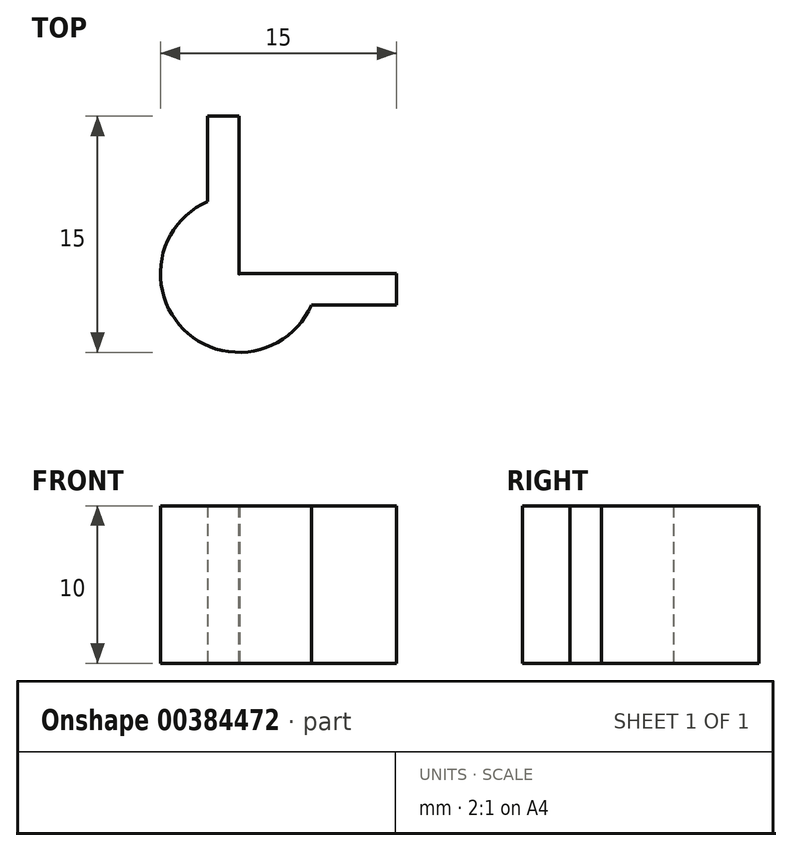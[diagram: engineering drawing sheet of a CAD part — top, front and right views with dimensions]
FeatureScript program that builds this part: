
annotation { "Feature Type Name" : "Feature", "Feature Type Description" : "" }
export const myFeature = defineFeature(function(context is Context, id is Id, definition is map)
    precondition{}
    {
        {
            var Q0;
            Q0=qCreatedBy(makeId("Top.planeOp"),FACE);
            var sketch = newSketch(context, id + "F0", { "sketchPlane" : qUnion([Q0])});
            skLineSegment(sketch, "E0.bottom", {"start": v(0, 0) * mm, "end": v(0, 0) * mm});
            skLineSegment(sketch, "E0.top", {"start": v(0, 0) * mm, "end": v(0, 0) * mm});
            skLineSegment(sketch, "E0.left", {"start": v(0, 0) * mm, "end": v(0, 0) * mm});
            skLineSegment(sketch, "E0.right", {"start": v(0, 0) * mm, "end": v(0, 0) * mm});
            skLineSegment(sketch, "E1.bottom", {"start": v(10, -2) * mm, "end": v(0, -2) * mm});
            skLineSegment(sketch, "E1.top", {"start": v(10, 0) * mm, "end": v(0, 0) * mm});
            skLineSegment(sketch, "E1.left", {"start": v(10, -2) * mm, "end": v(10, 0) * mm});
            skLineSegment(sketch, "E1.right", {"start": v(0, -2) * mm, "end": v(0, 0) * mm});
            skLineSegment(sketch, "E2.bottom", {"start": v(0, 0) * mm, "end": v(-2, 0) * mm});
            skLineSegment(sketch, "E2.top", {"start": v(0, 10) * mm, "end": v(-2, 10) * mm});
            skLineSegment(sketch, "E2.left", {"start": v(0, 0) * mm, "end": v(0, 10) * mm});
            skLineSegment(sketch, "E2.right", {"start": v(-2, 0) * mm, "end": v(-2, 10) * mm});
            skCircle(sketch, "E3", {"center": v(0, 0) * mm, "radius": 0.02 * mm});
            skCircle(sketch, "E4", {"center": v(0, 0) * mm, "radius": 5 * mm});
            skSolve(sketch);
        }
        {
            var Q0;
            {var subQ0=sQuery(id+"F0.wireOp",EDGE,"E2.top");Q0=makeQuery(id+"F0.imprint","IMPRINT",FACE,{"disambiguationData":[TD([[makeQuery(id+"F0.imprint","IMPRINT",EDGE,{"derivedFrom":subQ0}),1.0]])]});}
            var Q1;
            {var subQ0=sQuery(id+"F0.wireOp",EDGE,"E1.left");Q1=makeQuery(id+"F0.imprint","IMPRINT",FACE,{"disambiguationData":[TD([[makeQuery(id+"F0.imprint","IMPRINT",EDGE,{"derivedFrom":subQ0}),1.0]])]});}
            var Q2;
            {var subQ3=sQuery(id+"F0.wireOp",EDGE,"E1.right");var subQ7=sQuery(id+"F0.wireOp",EDGE,"E1.bottom");var subQ8=makeQuery(id+"F0.imprint","INTERSECT",VERTEX,{"derivedFrom":[subQ7,subQ3]});Q2=makeQuery(id+"F0.imprint","IMPRINT",FACE,{"disambiguationData":[TD([[makeQuery(id+"F0.imprint","IMPRINT",EDGE,{"disambiguationData":[TD([[subQ8,1.0]])],"derivedFrom":subQ7}),-1.0]])]});}
            var Q3;
            {var subQ1=sQuery(id+"F0.wireOp",EDGE,"E2.bottom");var subQ7=sQuery(id+"F0.wireOp",EDGE,"E2.right");var subQ8=makeQuery(id+"F0.imprint","INTERSECT",VERTEX,{"derivedFrom":[subQ1,subQ7]});Q3=makeQuery(id+"F0.imprint","IMPRINT",FACE,{"disambiguationData":[TD([[makeQuery(id+"F0.imprint","IMPRINT",EDGE,{"disambiguationData":[TD([[subQ8,1.0]])],"derivedFrom":subQ1}),-1.0]])]});}
            var Q4;
            {var subQ7=sQuery(id+"F0.wireOp",EDGE,"E1.right");var subQ8=sQuery(id+"F0.wireOp",EDGE,"E1.bottom");var subQ9=makeQuery(id+"F0.imprint","INTERSECT",VERTEX,{"derivedFrom":[subQ8,subQ7]});Q4=makeQuery(id+"F0.imprint","IMPRINT",FACE,{"disambiguationData":[TD([[makeQuery(id+"F0.imprint","IMPRINT",EDGE,{"disambiguationData":[TD([[subQ9,1.0]])],"derivedFrom":subQ8}),1.0]])]});}
            extrude(context, id + "F1", {"entities" : qUnion([Q0, Q1, Q2, Q3, Q4]), "depth" : 10 * mm});
        }
    });
